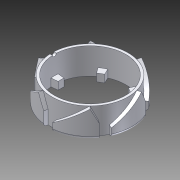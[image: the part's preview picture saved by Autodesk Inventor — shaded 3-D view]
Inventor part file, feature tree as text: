
AUTODESK INVENTOR PART (.ipt)
format: ipt  version: 2012 (Build 160160000, 160)  size: 327,168 bytes
history: native  units: mm
features: extrude x10, sketch x8, pattern_circular x6, helix x6, mirror x4, fillet x2, chamfer x1
ambient origin geometry x8: Origin, YZ Plane, XZ Plane, XY Plane, X Axis, Y Axis, Z Axis, Center Point
bodies: Solid1 (feature_tree)
feature tree (37):
  sketch  "Sketch1"  dims[d0=64.0mm d1=54.2mm]
  extrude  "Extrusion1"  Depth=54.2mm
  extrude  "Extrusion2"  Depth=58.0mm
  extrude  "Extrusion3"  Depth=20.0mm TaperAngle=0.0deg
  extrude  "Extrusion4"  Depth=4.0mm
  mirror  "Mirror1"
  fillet  "Fillet2"  Radius=4.0mm
  extrude  "Extrusion5"  Depth=16.0mm
  mirror  "Mirror2"
  pattern_circular  "Circular Pattern3"  Count=6 Angle=360.0deg
  sketch  "Sketch3"  dims[d4=1.0mm d5=0.0mm d6=20.0mm d7=0.0mm]
  extrude  "Extrusion6"  Depth=30.0mm TaperAngle=360.0deg
  mirror  "Mirror3"
  pattern_circular  "Circular Pattern4"  [2 undecoded]
  extrude  "Extrusion7"  Depth=5.8mm TaperAngle=0.0deg
  mirror  "Mirror4"
  pattern_circular  "Circular Pattern5"  Count=6 Angle=360.0deg
  chamfer  "Chamfer1"  Distance=44.1mm
  pattern_circular  "Circular Pattern2"  [2 undecoded]
  fillet  "Fillet3"  Radius=60.0mm
  helix  "Coil1"  [1 undecoded]
  extrude  "Extrusion8"  Depth=2.0mm
  sketch  "Sketch5"  dims[d17=2.0mm d18=16.0mm d19=60.0mm d20=360.0deg]
  helix  "Coil2"  [1 undecoded]
  helix  "Coil3"  [1 undecoded]
  helix  "Coil4"  [1 undecoded]
  extrude  "Extrusion9"  Depth=26.0mm
  pattern_circular  "Circular Pattern6"  [2 undecoded]
  sketch  "Sketch7"  dims[d27=40.1mm]
  helix  "Coil5"  [1 undecoded]
  helix  "Coil6"  [1 undecoded]
  pattern_circular  "Circular Pattern7"  Count=6 Angle=360.0deg
  extrude  "Extrusion10"  Depth=1.047198mm
  sketch  "Sketch2"  dims[d2=50.0mm d3=58.0mm]
  sketch  "Sketch4"  dims[d8=4.0mm d9=0.0mm d10=4.0mm d11=4.0mm d12=0.0mm]
  sketch  "Sketch6"  dims[d22=3.0mm d23=0.0mm d24=30.0mm d25=360.0deg]
  sketch  "Sketch8"  dims[d28=49.0mm d29=1.012291mm d30=5.8mm d31=0.0mm d32=60.0mm d33=360.0deg d35=44.1mm d36=55.0mm d37=1.012291mm d38=5.8mm d39=0.0mm d40=60.0mm d41=360.0deg d43=16.0mm d44=17.0mm d45=45.0deg d46=2.0mm d47=4.0mm d48=20.0mm d49=16.0mm d50=1.666667mm d51=0.0mm d52=90.0deg d53=90.0deg d54=0.0mm d55=0.0mm d56=10.0mm d57=0.0mm d58=4.0mm d59=26.0mm d60=20.0mm d61=18.0mm d62=1.25mm d63=0.0mm d64=90.0deg d65=90.0deg d66=0.0mm d67=0.0mm d68=20.0mm d69=20.0mm d70=1.666667mm d71=0.0mm d72=90.0deg d73=90.0deg d74=0.0mm d75=0.0mm d76=4.0mm d77=20.0mm d78=18.0mm d79=0.416667mm d80=0.0mm d81=90.0deg d82=90.0deg d83=0.0mm d84=0.0mm d86=2.094395mm d87=10.0mm d88=0.0mm d89=60.0mm d90=360.0deg d92=1.047198mm d93=29.0mm d94=22.0mm d95=10.0mm d96=16.0mm d97=1.25mm d98=0.0mm d99=90.0deg d100=90.0deg d101=0.0mm d102=0.0mm d103=16.0mm d104=10.0mm d105=16.0mm d106=0.416667mm d107=0.0mm d108=90.0deg d109=90.0deg d110=0.0mm d111=0.0mm d112=60.0mm d113=360.0deg d115=18.0mm d116=3.0mm d117=20.0mm d118=10.0mm d119=0.0mm d120=30.0deg]
note: 12 required parameter values undecoded (feature->parameter linkage not recoverable at this tier; creation-order binding heuristic only, values carry confidence <= 0.55)
